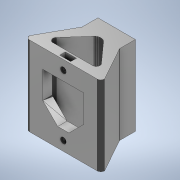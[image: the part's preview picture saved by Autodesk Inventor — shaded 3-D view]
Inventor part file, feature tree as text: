
AUTODESK INVENTOR PART (.ipt)
format: ipt  version: 2021 (Build 250183000, 183)  size: 1,994,240 bytes
history: native  units: in
note: dims shown in document units (in); Inventor stores cm internally (conversion verified against a paired STEP export)
features: other x3, plane x2, split x2, extrude x2, sketch x2, move_body x1, boolean_combine x1
ambient origin geometry x8: Origin, YZ Plane, XZ Plane, XY Plane, X Axis, Y Axis, Z Axis, Center Point
bodies: Solid1 (feature_tree), Solid2 (feature_tree), Solid3 (feature_tree)
feature tree (13):
  other  "PenSlider.ipt"
  plane  "Work Plane1"
  split  "Split1"
  plane  "Work Plane2"
  split  "Split2"
  move_body  "Move Body1"
  boolean_combine  "Combine1"
  extrude  "Extrusion3"  [1 undecoded]
  extrude  "Extrusion4"  Depth=0.3937in TaperAngle=0.0deg
  other  "Solid3::PenSlider.ipt"
  other  "TaggingFeature1"
  sketch  "Sketch4"  dims[d0=0.3937in d1=-0.709in]
  sketch  "Sketch5"  dims[d2=-1.125in d3=0.0in d4=0.416in d5=0.0in d16=0.1969in d17=0.3937in d18=0.0in d19=0.3937in d20=0.0in]
note: 1 required parameter value undecoded (feature->parameter linkage not recoverable at this tier; creation-order binding heuristic only, values carry confidence <= 0.55)
